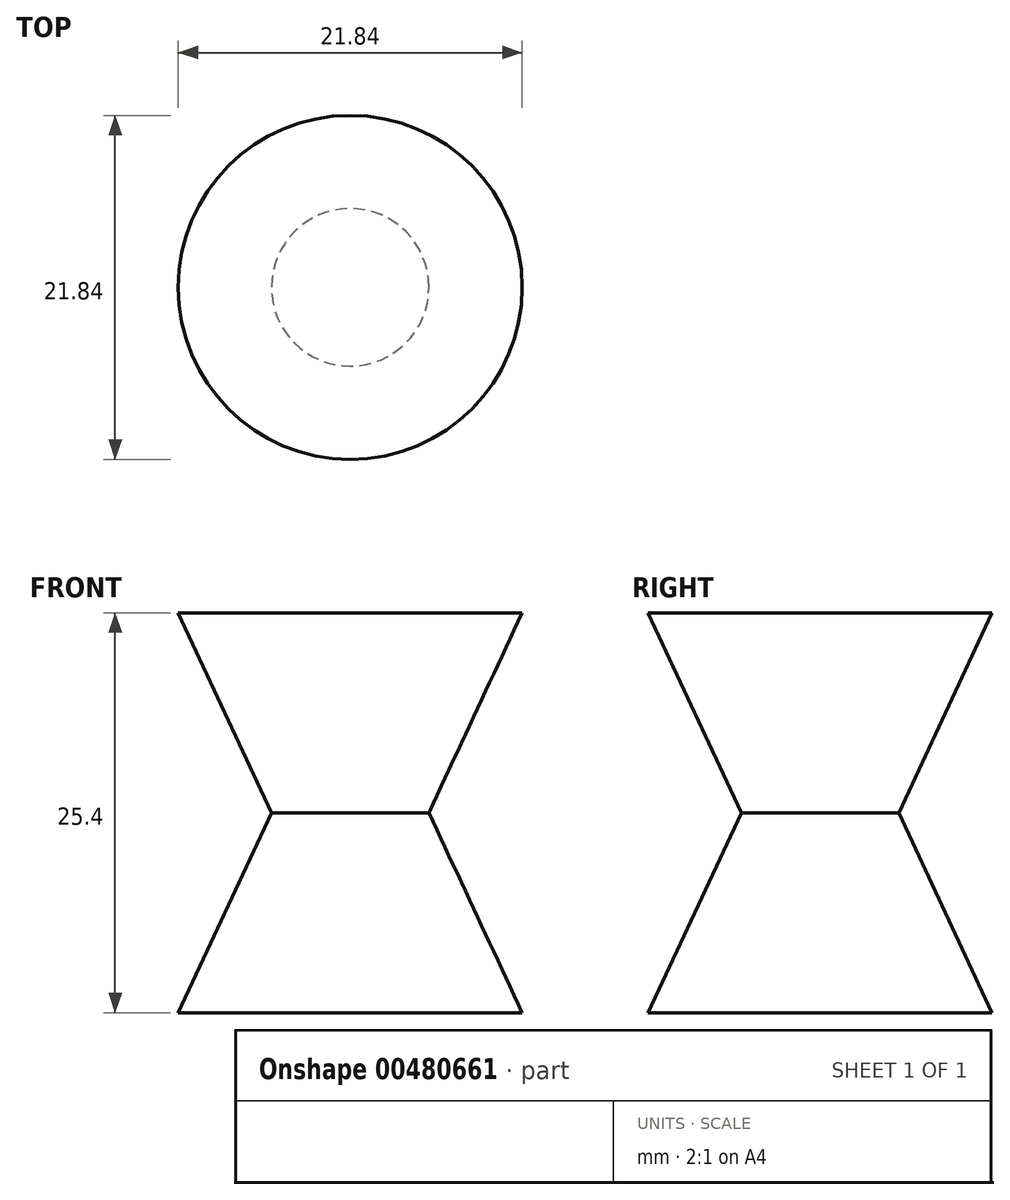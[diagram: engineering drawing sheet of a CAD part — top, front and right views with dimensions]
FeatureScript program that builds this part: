
annotation { "Feature Type Name" : "Feature", "Feature Type Description" : "" }
export const myFeature = defineFeature(function(context is Context, id is Id, definition is map)
    precondition{}
    {
        {
            var Q0;
            Q0=qCreatedBy(makeId("Top.planeOp"),FACE);
            var sketch = newSketch(context, id + "F0", { "sketchPlane" : qUnion([Q0])});
            skCircle(sketch, "E0", {"center": v(0, 0) * mm, "radius": 5 * mm});
            skSolve(sketch);
        }
        {
            var Q0;
            Q0=makeQuery(id+"F0.imprint","IMPRINT",FACE,{"disambiguationData":[TD([[makeQuery(id+"F0.imprint","IMPRINT",EDGE,{"derivedFrom":sQuery(id+"F0.wireOp",EDGE,"E0")}),1.0]])]});
            extrude(context, id + "F1", {"entities" : qUnion([Q0]), "endBound" : BoundingType.SYMMETRIC, "depth" : 25.4 * mm, "hasDraft" : true, "draftAngle" : 25 * degree});
        }
    });
